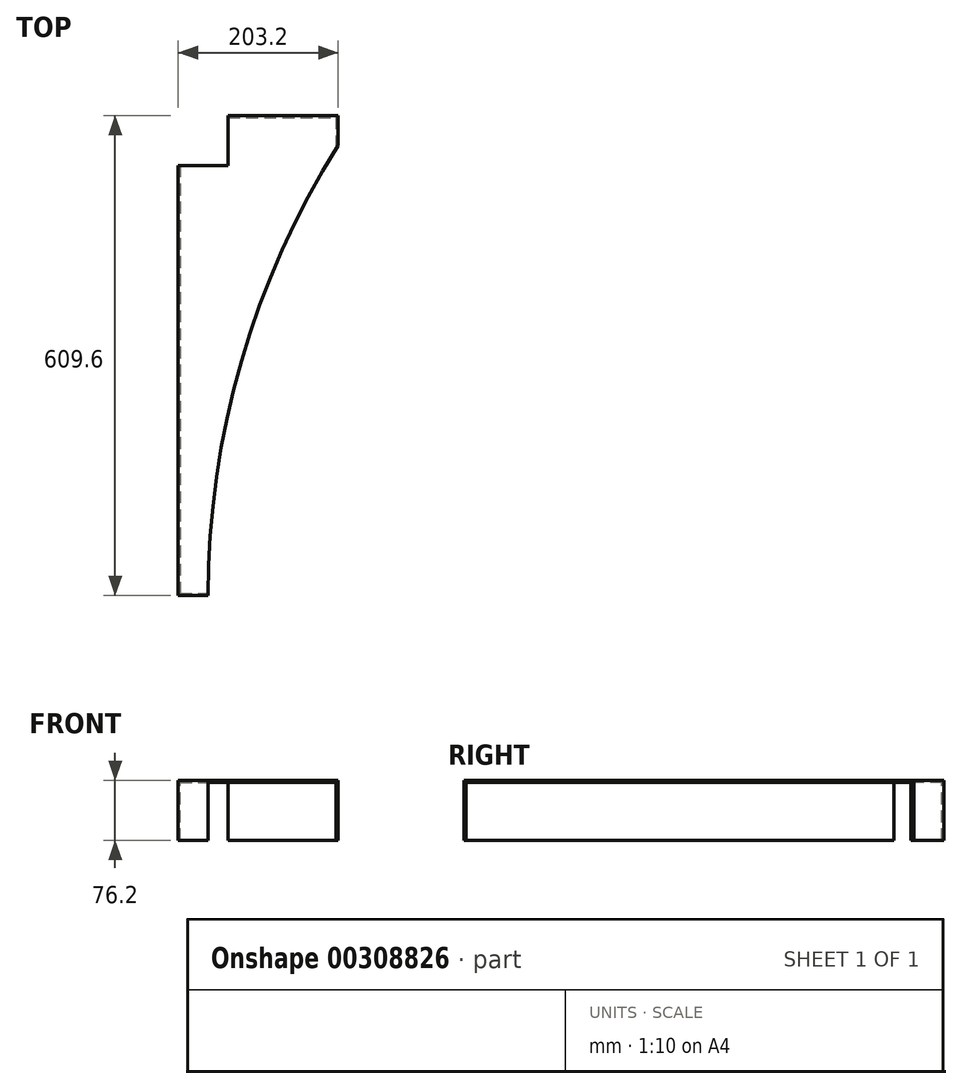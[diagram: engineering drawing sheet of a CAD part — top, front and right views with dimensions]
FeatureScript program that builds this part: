
annotation { "Feature Type Name" : "Feature", "Feature Type Description" : "" }
export const myFeature = defineFeature(function(context is Context, id is Id, definition is map)
    precondition{}
    {
        {
            var Q0;
            Q0=qCreatedBy(makeId("Top.planeOp"),FACE);
            var sketch = newSketch(context, id + "F0", { "sketchPlane" : qUnion([Q0])});
            skLineSegment(sketch, "E0", {"start": v(63.5, 0) * mm, "end": v(203.2, 0) * mm});
            skLineSegment(sketch, "E1", {"start": v(0, -63.5) * mm, "end": v(0, -609.6) * mm});
            skLineSegment(sketch, "E2", {"start": v(203.2, 0) * mm, "end": v(203.2, -38.1) * mm});
            skLineSegment(sketch, "E3", {"start": v(0, -609.6) * mm, "end": v(38.1, -609.6) * mm});
            skArc(sketch, "E4", {"start": v(203.2, -38.1) * mm, "mid": v(80.2, -312.17) * mm, "end": v(38.1, -609.6) * mm});
            skLineSegment(sketch, "E5", {"start": v(63.5, 0) * mm, "end": v(63.5, -63.5) * mm});
            skLineSegment(sketch, "E6", {"start": v(63.5, -63.5) * mm, "end": v(0, -63.5) * mm});
            skSolve(sketch);
        }
        {
            var Q0;
            Q0 = qSketchRegion(id + "F0", true);
            extrude(context, id + "F1", {"entities" : qUnion([Q0]), "oppositeDirection" : true, "depth" : 76.2 * mm});
        }
        {
            var Q0;
            Q0=makeQuery(id+"F1.opExtrude","CAP_FACE",FACE,{"disambiguationData":[OSD([sQuery(id+"F0.wireOp",EDGE,"E0"),sQuery(id+"F0.wireOp",EDGE,"E1"),sQuery(id+"F0.wireOp",EDGE,"E2"),sQuery(id+"F0.wireOp",EDGE,"E3"),sQuery(id+"F0.wireOp",EDGE,"E4"),sQuery(id+"F0.wireOp",EDGE,"E5"),sQuery(id+"F0.wireOp",EDGE,"E6")])],"isStart":false});
            var Q1;
            Q1=makeQuery(id+"F1.opExtrude","SWEPT_FACE",FACE,{"disambiguationData":[OSD([sQuery(id+"F0.wireOp",EDGE,"E4")])]});
            var Q2;
            Q2=makeQuery(id+"F1.opExtrude","SWEPT_FACE",FACE,{"disambiguationData":[OSD([sQuery(id+"F0.wireOp",EDGE,"E6")])]});
            var Q3;
            Q3=makeQuery(id+"F1.opExtrude","SWEPT_FACE",FACE,{"disambiguationData":[OSD([sQuery(id+"F0.wireOp",EDGE,"E5")])]});
            shell(context, id + "F2", {"entities" : qUnion([Q0, Q1, Q2, Q3]), "thickness" : 2.54 * mm});
        }
    });
